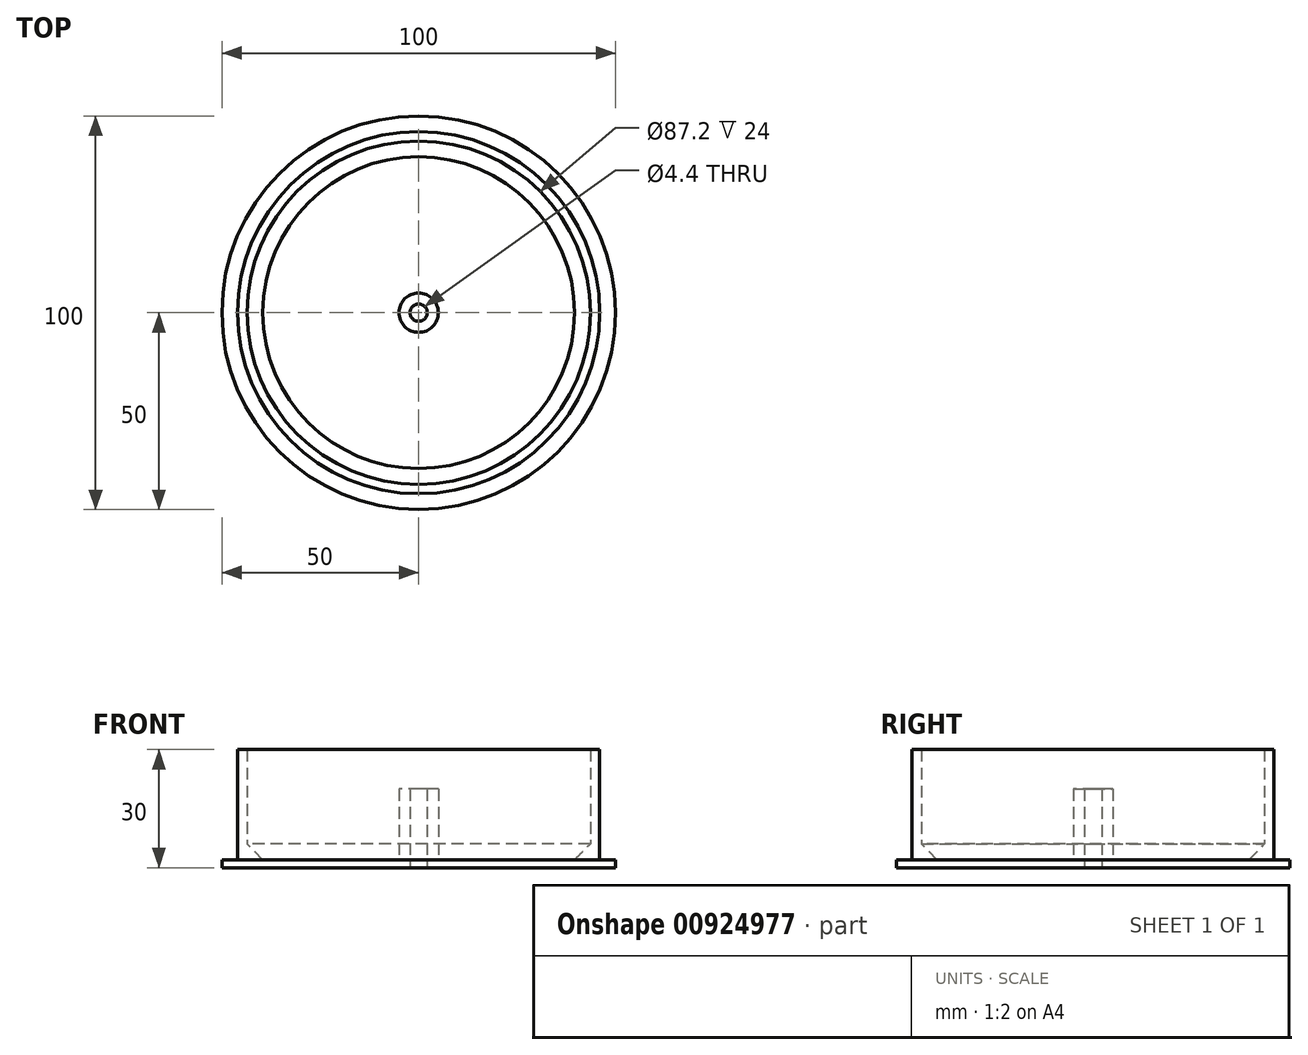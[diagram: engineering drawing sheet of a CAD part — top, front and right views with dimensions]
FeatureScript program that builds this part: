
annotation { "Feature Type Name" : "Feature", "Feature Type Description" : "" }
export const myFeature = defineFeature(function(context is Context, id is Id, definition is map)
    precondition{}
    {
        {
            var Q0;
            Q0=qCreatedBy(makeId("Top.planeOp"),FACE);
            var sketch = newSketch(context, id + "F0", { "sketchPlane" : qUnion([Q0])});
            skCircle(sketch, "E0", {"center": v(0, 0) * mm, "radius": 43.6 * mm});
            skCircle(sketch, "E1", {"center": v(0, 0) * mm, "radius": 46 * mm});
            skCircle(sketch, "E2", {"center": v(0, 0) * mm, "radius": 50 * mm});
            skCircle(sketch, "E3", {"center": v(0, 0) * mm, "radius": 2.2 * mm});
            skCircle(sketch, "E4", {"center": v(0, 0) * mm, "radius": 5 * mm});
            skSolve(sketch);
        }
        {
            var Q0;
            Q0=makeQuery(id+"F0.imprint","IMPRINT",FACE,{"disambiguationData":[TD([[makeQuery(id+"F0.imprint","IMPRINT",EDGE,{"derivedFrom":sQuery(id+"F0.wireOp",EDGE,"E0")}),1.0]])]});
            var Q1;
            Q1=makeQuery(id+"F0.imprint","IMPRINT",FACE,{"disambiguationData":[TD([[makeQuery(id+"F0.imprint","IMPRINT",EDGE,{"derivedFrom":sQuery(id+"F0.wireOp",EDGE,"E1")}),-1.0]])]});
            var Q2;
            Q2=makeQuery(id+"F0.imprint","IMPRINT",FACE,{"disambiguationData":[TD([[makeQuery(id+"F0.imprint","IMPRINT",EDGE,{"derivedFrom":sQuery(id+"F0.wireOp",EDGE,"E0")}),-1.0]])]});
            extrude(context, id + "F1", {"entities" : qUnion([Q0, Q1, Q2]), "depth" : 2 * mm, "offsetDistance" : 25 * mm});
        }
        {
            var Q0;
            Q0=makeQuery(id+"F0.imprint","IMPRINT",FACE,{"disambiguationData":[TD([[makeQuery(id+"F0.imprint","IMPRINT",EDGE,{"derivedFrom":sQuery(id+"F0.wireOp",EDGE,"E0")}),-1.0]])]});
            extrude(context, id + "F2", {"entities" : qUnion([Q0]), "operationType" : NewBodyOperationType.ADD, "depth" : 30 * mm, "offsetDistance" : 25 * mm});
        }
        {
            var Q0;
            Q0=makeQuery(id+"F0.imprint","IMPRINT",FACE,{"disambiguationData":[TD([[makeQuery(id+"F0.imprint","IMPRINT",EDGE,{"derivedFrom":sQuery(id+"F0.wireOp",EDGE,"E3")}),-1.0]])]});
            extrude(context, id + "F3", {"entities" : qUnion([Q0]), "operationType" : NewBodyOperationType.ADD, "depth" : 20 * mm, "offsetDistance" : 25 * mm});
        }
        {
            var Q0;
            Q0=makeQuery(id+"F1.opExtrude","CAP_EDGE",EDGE,{"disambiguationData":[OSD([sQuery(id+"F0.wireOp",EDGE,"E4")])],"isStart":false});
            var Q1;
            Q1=makeQuery(id+"F2.boolean.opBoolean","INTERSECT",EDGE,{"derivedFrom":[makeQuery(id+"F1.opExtrude","CAP_FACE",FACE,{"disambiguationData":[OSD([sQuery(id+"F0.wireOp",EDGE,"E2"),sQuery(id+"F0.wireOp",EDGE,"E4")])],"isStart":false}),makeQuery(id+"F2.opExtrude","SWEPT_FACE",FACE,{"disambiguationData":[OSD([sQuery(id+"F0.wireOp",EDGE,"E0")])]})]});
            chamfer(context, id + "F4", {"entities" : qUnion([Q0, Q1]), "width" : 4 * mm, "tangentPropagation" : true});
        }
    });
